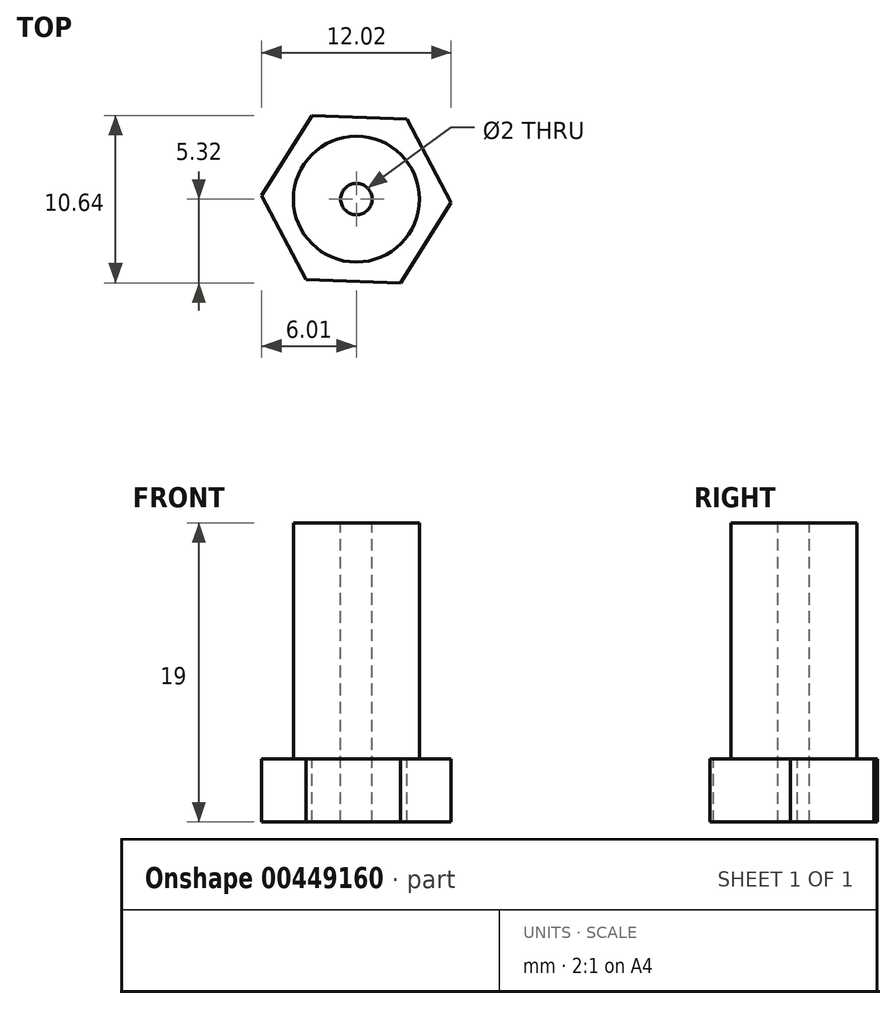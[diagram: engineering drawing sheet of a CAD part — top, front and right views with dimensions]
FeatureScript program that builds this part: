
annotation { "Feature Type Name" : "Feature", "Feature Type Description" : "" }
export const myFeature = defineFeature(function(context is Context, id is Id, definition is map)
    precondition{}
    {
        {
            var Q0;
            Q0=qCreatedBy(makeId("Top.planeOp"),FACE);
            var sketch = newSketch(context, id + "F0", { "sketchPlane" : qUnion([Q0])});
            skCircle(sketch, "E0", {"center": v(0, 0) * mm, "radius": 4 * mm});
            skCircle(sketch, "E1.cCircle", {"center": v(0, 0) * mm, "radius": 5.21 * mm, "construction": true});
            skLineSegment(sketch, "E1.0", {"start": v(3.2, 5.1) * mm, "end": v(6.01, -0.22) * mm});
            skLineSegment(sketch, "E1.1", {"start": v(6.01, -0.22) * mm, "end": v(2.81, -5.32) * mm});
            skLineSegment(sketch, "E1.2", {"start": v(2.81, -5.32) * mm, "end": v(-3.2, -5.1) * mm});
            skLineSegment(sketch, "E1.3", {"start": v(-3.2, -5.1) * mm, "end": v(-6.01, 0.22) * mm});
            skLineSegment(sketch, "E1.4", {"start": v(-6.01, 0.22) * mm, "end": v(-2.81, 5.32) * mm});
            skLineSegment(sketch, "E1.5", {"start": v(-2.81, 5.32) * mm, "end": v(3.2, 5.1) * mm});
            skPoint(sketch, "E1.0.midPoint", {"position": v(4.6, 2.44) * mm});
            skSolve(sketch);
        }
        {
            var Q0;
            Q0=makeQuery(id+"F0.imprint","IMPRINT",FACE,{"disambiguationData":[TD([[makeQuery(id+"F0.imprint","IMPRINT",EDGE,{"derivedFrom":sQuery(id+"F0.wireOp",EDGE,"E0")}),1.0]])]});
            extrude(context, id + "F1", {"entities" : qUnion([Q0]), "depth" : 15 * mm});
        }
        {
            var Q0;
            Q0=makeQuery(id+"F1.opExtrude","CAP_FACE",FACE,{"disambiguationData":[OSD([sQuery(id+"F0.wireOp",EDGE,"E0")])],"isStart":true});
            var Q1;
            Q1=makeQuery(id+"F0.imprint","IMPRINT",FACE,{"disambiguationData":[TD([[makeQuery(id+"F0.imprint","IMPRINT",EDGE,{"derivedFrom":sQuery(id+"F0.wireOp",EDGE,"E0")}),-1.0]])]});
            extrude(context, id + "F2", {"entities" : qUnion([Q0, Q1]), "operationType" : NewBodyOperationType.ADD, "depth" : 4 * mm});
        }
        {
            var Q0;
            Q0=makeQuery(id+"F1.opExtrude","CAP_FACE",FACE,{"disambiguationData":[OSD([sQuery(id+"F0.wireOp",EDGE,"E0")])],"isStart":false});
            var sketch = newSketch(context, id + "F3", { "sketchPlane" : qUnion([Q0])});
            skPoint(sketch, "E2.0", {"position": v(0, 0) * mm});
            skCircle(sketch, "E3", {"center": v(0, 0) * mm, "radius": 1 * mm});
            skSolve(sketch);
        }
        {
            var Q0;
            Q0=makeQuery(id+"F3.imprint","IMPRINT",FACE,{"disambiguationData":[TD([[makeQuery(id+"F3.imprint","IMPRINT",EDGE,{"derivedFrom":sQuery(id+"F3.wireOp",EDGE,"E3")}),1.0]])]});
            extrude(context, id + "F4", {"entities" : qUnion([Q0]), "operationType" : NewBodyOperationType.REMOVE, "endBound" : BoundingType.THROUGH_ALL, "oppositeDirection" : true, "depth" : 25 * mm});
        }
    });
